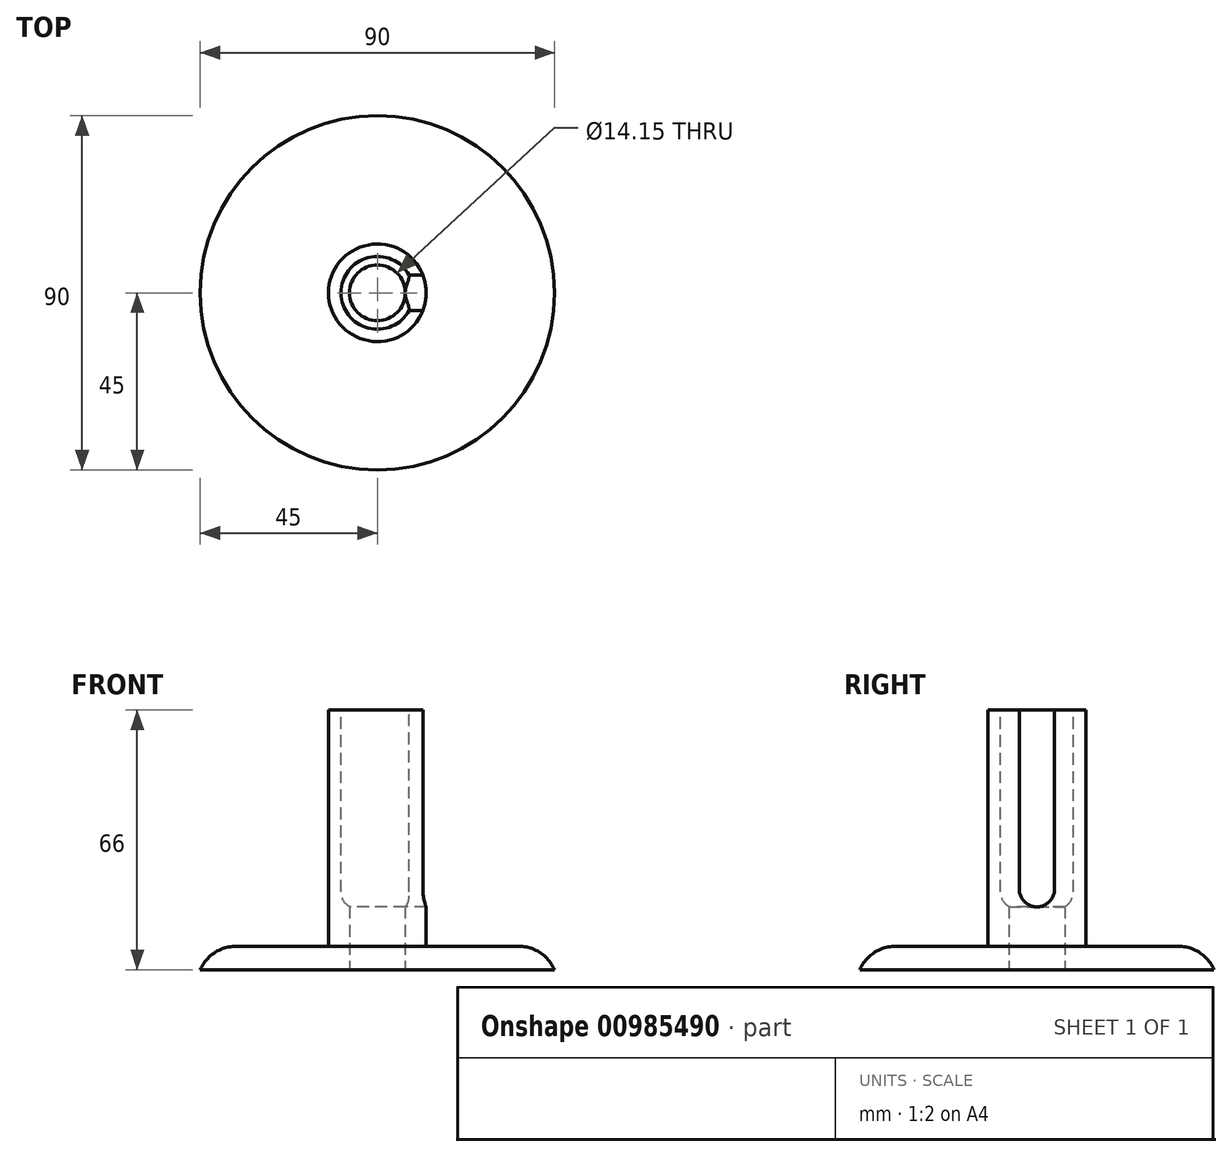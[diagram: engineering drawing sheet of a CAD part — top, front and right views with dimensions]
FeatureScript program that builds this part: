
annotation { "Feature Type Name" : "Feature", "Feature Type Description" : "" }
export const myFeature = defineFeature(function(context is Context, id is Id, definition is map)
    precondition{}
    {
        {
            var Q0;
            Q0=qCreatedBy(makeId("Top.planeOp"),FACE);
            var sketch = newSketch(context, id + "F0", { "sketchPlane" : qUnion([Q0])});
            skCircle(sketch, "E0", {"center": v(0, 0) * mm, "radius": 45 * mm});
            skCircle(sketch, "E1", {"center": v(0, 0) * mm, "radius": 7.08 * mm});
            skSolve(sketch);
        }
        {
            var Q0;
            Q0=makeQuery(id+"F0.imprint","IMPRINT",FACE,{"disambiguationData":[TD([[makeQuery(id+"F0.imprint","IMPRINT",EDGE,{"derivedFrom":sQuery(id+"F0.wireOp",EDGE,"E0")}),1.0]])]});
            extrude(context, id + "F1", {"entities" : qUnion([Q0]), "depth" : 6 * mm, "offsetDistance" : 25 * mm});
        }
        {
            var Q0;
            Q0=makeQuery(id+"F1.opExtrude","CAP_FACE",FACE,{"disambiguationData":[OSD([sQuery(id+"F0.wireOp",EDGE,"E0"),sQuery(id+"F0.wireOp",EDGE,"E1")])],"isStart":false});
            var sketch = newSketch(context, id + "F2", { "sketchPlane" : qUnion([Q0])});
            skCircle(sketch, "E2", {"center": v(0, 0) * mm, "radius": 12.4 * mm});
            skSolve(sketch);
        }
        {
            var Q0;
            Q0=makeQuery(id+"F2.imprint","IMPRINT",FACE,{"disambiguationData":[TD([[makeQuery(id+"F2.imprint","IMPRINT",EDGE,{"derivedFrom":sQuery(id+"F2.wireOp",EDGE,"E2")}),1.0]])]});
            extrude(context, id + "F3", {"entities" : qUnion([Q0]), "operationType" : NewBodyOperationType.ADD, "depth" : 60 * mm, "offsetDistance" : 25 * mm});
        }
        {
            var Q0;
            Q0=makeQuery(id+"F3.opExtrude","CAP_FACE",FACE,{"disambiguationData":[OSD([sQuery(id+"F0.wireOp",EDGE,"E1"),sQuery(id+"F2.wireOp",EDGE,"E2")])],"isStart":false});
            var sketch = newSketch(context, id + "F4", { "sketchPlane" : qUnion([Q0])});
            skCircle(sketch, "E3", {"center": v(0, 0) * mm, "radius": 9.25 * mm});
            skSolve(sketch);
        }
        {
            var Q0;
            Q0=makeQuery(id+"F4.imprint","IMPRINT",FACE,{"disambiguationData":[TD([[makeQuery(id+"F4.imprint","IMPRINT",EDGE,{"derivedFrom":sQuery(id+"F4.wireOp",EDGE,"E3")}),1.0]])]});
            extrude(context, id + "F5", {"entities" : qUnion([Q0]), "operationType" : NewBodyOperationType.REMOVE, "oppositeDirection" : true, "depth" : 50 * mm, "offsetDistance" : 25 * mm});
        }
        {
            var Q0;
            Q0=makeQuery(id+"F3.opExtrude","CAP_FACE",FACE,{"disambiguationData":[OSD([sQuery(id+"F0.wireOp",EDGE,"E1"),sQuery(id+"F2.wireOp",EDGE,"E2")])],"isStart":false});
            var sketch = newSketch(context, id + "F6", { "sketchPlane" : qUnion([Q0])});
            skLineSegment(sketch, "E4", {"start": v(0, 4.5) * mm, "end": v(16.88, 4.5) * mm});
            skLineSegment(sketch, "E5.MirrorCS", {"start": v(0, -4.5) * mm, "end": v(16.88, -4.5) * mm});
            skLineSegment(sketch, "E6", {"start": v(16.88, 4.5) * mm, "end": v(16.88, -4.5) * mm});
            skLineSegment(sketch, "E7", {"start": v(0, 4.5) * mm, "end": v(0, -4.5) * mm});
            skSolve(sketch);
        }
        {
            var Q0;
            {var subQ0=sQuery(id+"F6.wireOp",EDGE,"E4");var subQ1=makeQuery(id+"F3.opExtrude","CAP_EDGE",EDGE,{"disambiguationData":[OSD([sQuery(id+"F2.wireOp",EDGE,"E2")])],"isStart":false});var subQ2=makeQuery(id+"F6.imprint","INTERSECT",VERTEX,{"derivedFrom":[subQ1,subQ0]});Q0=makeQuery(id+"F6.imprint","IMPRINT",FACE,{"disambiguationData":[TD([[makeQuery(id+"F6.imprint","IMPRINT",EDGE,{"disambiguationData":[TD([[subQ2,1.0]])],"derivedFrom":subQ0}),-1.0]])]});}
            extrude(context, id + "F7", {"entities" : qUnion([Q0]), "operationType" : NewBodyOperationType.REMOVE, "oppositeDirection" : true, "depth" : 50 * mm, "offsetDistance" : 25 * mm});
        }
        {
            var Q0;
            Q0=makeQuery(id+"F1.opExtrude","CAP_EDGE",EDGE,{"disambiguationData":[OSD([sQuery(id+"F0.wireOp",EDGE,"E0")])],"isStart":false});
            var Q1;
            Q1=makeQuery(id+"F3.opExtrude","CAP_EDGE",EDGE,{"disambiguationData":[OSD([sQuery(id+"F2.wireOp",EDGE,"E2")])],"isStart":true});
            fillet(context, id + "F8", {"entities" : qUnion([Q0, Q1]), "radius" : 10 * mm, "tangentPropagation" : true, "allowEdgeOverflow" : false});
        }
        {
            var Q0;
            Q0=makeQuery(id+"F7.boolean.opBoolean","COPY",EDGE,{"derivedFrom":makeQuery(id+"F7.opExtrude","CAP_EDGE",EDGE,{"disambiguationData":[OSD([sQuery(id+"F6.wireOp",EDGE,"E4")])],"isStart":false})});
            var Q1;
            Q1=makeQuery(id+"F7.boolean.opBoolean","COPY",EDGE,{"derivedFrom":makeQuery(id+"F7.opExtrude","CAP_EDGE",EDGE,{"disambiguationData":[OSD([sQuery(id+"F6.wireOp",EDGE,"E5.MirrorCS")])],"isStart":false})});
            var Q2;
            Q2=makeQuery(id+"F5.boolean.opBoolean","COPY",EDGE,{"derivedFrom":makeQuery(id+"F5.opExtrude","CAP_EDGE",EDGE,{"disambiguationData":[OSD([sQuery(id+"F4.wireOp",EDGE,"E3")])],"isStart":false})});
            fillet(context, id + "F9", {"entities" : qUnion([Q0, Q1, Q2]), "radius" : 4.5 * mm, "tangentPropagation" : true, "allowEdgeOverflow" : false});
        }
    });
